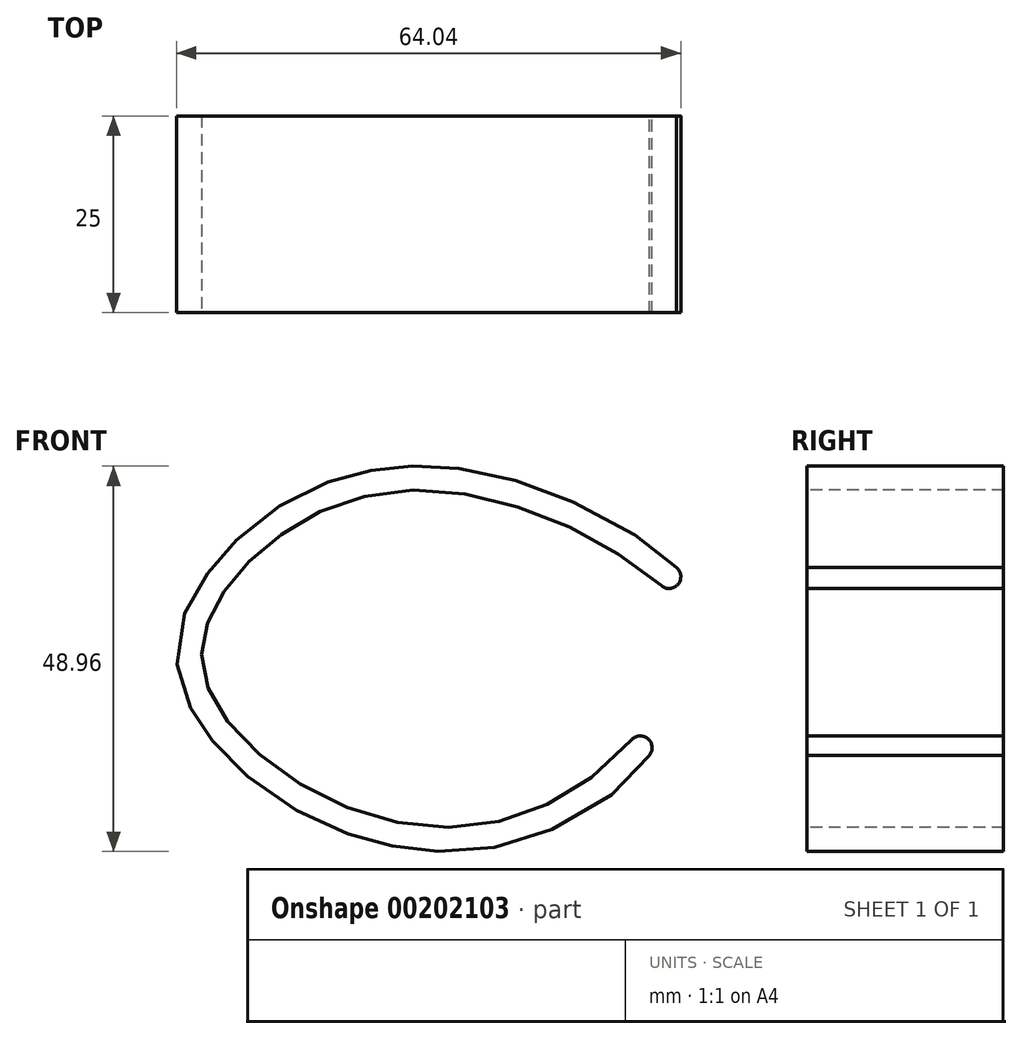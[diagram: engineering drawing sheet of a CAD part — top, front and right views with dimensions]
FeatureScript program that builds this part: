
annotation { "Feature Type Name" : "Feature", "Feature Type Description" : "" }
export const myFeature = defineFeature(function(context is Context, id is Id, definition is map)
    precondition{}
    {
        {
            var Q0;
            Q0=qCreatedBy(makeId("Front.planeOp"),FACE);
            var sketch = newSketch(context, id + "F0", { "sketchPlane" : qUnion([Q0])});
            skLineSegment(sketch, "E0", {"start": v(0, 0) * mm, "end": v(-40.05, -23.12) * mm, "construction": true});
            skLineSegment(sketch, "E1", {"start": v(0, 0) * mm, "end": v(58.93, -38.27) * mm, "construction": true});
            skPoint(sketch, "E2", {"position": v(0, 12) * mm});
            skPoint(sketch, "E3", {"position": v(34, 0) * mm});
            skPoint(sketch, "E4", {"position": v(-21, 0) * mm});
            skPoint(sketch, "E5", {"position": v(-23.38, -13.5) * mm});
            skPoint(sketch, "E6", {"position": v(0, -30) * mm});
            skPoint(sketch, "E7", {"position": v(30.2, -19.6) * mm});
            skFitSpline(sketch, "E8", {"points": [v(34, 0) * mm, v(0, 12) * mm, v(-21, 0) * mm, v(-23.38, -13.5) * mm, v(0, -30) * mm, v(30.2, -19.6) * mm], "startDerivative": vector(-116.77, 98.88) * mm, "endDerivative": vector(107.58, 124.48) * mm});
            skFitSpline(sketch, "E9.0", {"points": [v(35.94, 2.29) * mm, v(33.35, 4.48) * mm, v(28.98, 7.48) * mm, v(22.58, 10.7) * mm, v(17.58, 12.68) * mm, v(12.45, 14.14) * mm, v(8.15, 14.88) * mm, v(4.73, 15.15) * mm, v(2.19, 15.17) * mm, v(-0.33, 15.02) * mm, v(-2.78, 14.66) * mm, v(-5.14, 14.13) * mm, v(-8.19, 13.2) * mm, v(-11.75, 11.67) * mm, v(-15.6, 9.37) * mm, v(-19, 6.7) * mm, v(-21.43, 4.26) * mm, v(-23.1, 2.23) * mm, v(-24.6, 0.15) * mm, v(-26.14, -2.58) * mm, v(-27.29, -6.11) * mm, v(-27.53, -9.89) * mm, v(-26.85, -13.08) * mm, v(-25.75, -15.6) * mm, v(-24.7, -17.42) * mm, v(-23.43, -19.19) * mm, v(-21.5, -21.47) * mm, v(-18.64, -24.18) * mm, v(-14.64, -27.13) * mm, v(-10.18, -29.67) * mm, v(-6.18, -31.37) * mm, v(-2.87, -32.42) * mm, v(-0.34, -33.03) * mm, v(2.22, -33.45) * mm, v(5.63, -33.75) * mm, v(9.89, -33.65) * mm, v(14.9, -32.76) * mm, v(19.76, -31.1) * mm, v(25.9, -27.9) * mm, v(30.03, -24.38) * mm, v(32.46, -21.57) * mm]});
            skArc(sketch, "E10", {"start": v(32.46, -21.57) * mm, "mid": v(32.3, -19.45) * mm, "end": v(30.2, -19.6) * mm});
            skArc(sketch, "E11", {"start": v(34, 0) * mm, "mid": v(36.11, 0.18) * mm, "end": v(35.94, 2.29) * mm});
            skSolve(sketch);
        }
        {
            var Q0;
            Q0=makeQuery(id+"F0.imprint","IMPRINT",FACE,{"disambiguationData":[TD([[makeQuery(id+"F0.imprint","IMPRINT",EDGE,{"derivedFrom":sQuery(id+"F0.wireOp",EDGE,"E8")}),-1.0]])]});
            extrude(context, id + "F1", {"entities" : qUnion([Q0]), "depth" : 25 * mm});
        }
    });
